# Revit family: ПЛ-10_Eng
name_source: partatom
category: Duct Accessories
units: mm (PartAtom-declared; Revit-internal decimal feet)

## family parameters
Always vertical = Yes
Cut with Voids When Loaded = No
Part Type = Attaches To
Round Connector Dimension = Use Diameter
Shared = No
Work Plane-Based = No

## types (22) — shared parameters
00_20_Manufacturer = Vents
00_20_Name = Fire-resisting damper
Apparent Load = 7 VA
Casing Material = Steel, galvanized
Frequency = 50 Hz
Load Classification = HVAC
Maintenance zone material = <By Category>
Manufacturer = Vents
Number of Fase = 1
URL = https://ventilation-system.com
Voltage = 230 V
zero-valued in all types: Default Elevation

## per-type parameters (varying)
| type | B | D | D1 | D2 | Diameter | Height | L | Length | Maximum Air Flow | R | Weight | Width |
| PL-10-PVP230T-DN100/EI60 | 195 mm  [stored 0.639764 ft] | 99 mm  [stored 0.324803 ft] | 100 mm  [stored 0.328084 ft] | 95 mm | 99 mm  [stored 0.324803 ft] | 99 mm  [stored 0.324803 ft] | 300 mm | 300 mm | 32400.0 m³/h | 50 mm  [stored 0.164042 ft] | 2.90 kg | 195 mm  [stored 0.639764 ft] |
| PL-10-PVP230T-DN400/EI60 | 505 mm | 399 mm | 400 mm | 395 mm | 399 mm | 399 mm | 310 mm  [stored 1.01706 ft] | 310 mm  [stored 1.01706 ft] | 0.0 m³/h | 200 mm  [stored 0.656168 ft] | 9.90 kg | 505 mm |
| PL-10-PVP230T-DN100/EI120 | 195 mm  [stored 0.639764 ft] | 99 mm  [stored 0.324803 ft] | 100 mm  [stored 0.328084 ft] | 95 mm | 99 mm  [stored 0.324803 ft] | 99 mm  [stored 0.324803 ft] | 300 mm | 300 mm | 0.0 m³/h | 50 mm  [stored 0.164042 ft] | 2.90 kg | 195 mm  [stored 0.639764 ft] |
| PL-10-PVP230T-DN400/EI120 | 505 mm | 399 mm | 400 mm | 395 mm | 399 mm | 399 mm | 310 mm  [stored 1.01706 ft] | 310 mm  [stored 1.01706 ft] | 0.0 m³/h | 200 mm  [stored 0.656168 ft] | 9.90 kg | 505 mm |
| PL-10-PVP230T-DN125/EI60 | 215 mm | 124 mm  [stored 0.406824 ft] | 125 mm  [stored 0.410105 ft] | 120 mm  [stored 0.393701 ft] | 124 mm  [stored 0.406824 ft] | 124 mm  [stored 0.406824 ft] | 300 mm | 300 mm | 0.0 m³/h | 62 mm  [stored 0.203412 ft] | 3.10 kg | 215 mm |
| PL-10-PVP230T-DN125/EI120 | 215 mm | 124 mm  [stored 0.406824 ft] | 125 mm  [stored 0.410105 ft] | 120 mm  [stored 0.393701 ft] | 124 mm  [stored 0.406824 ft] | 124 mm  [stored 0.406824 ft] | 300 mm | 300 mm | 0.0 m³/h | 62 mm  [stored 0.203412 ft] | 3.10 kg | 215 mm |
| PL-10-PVP230T-DN150/EI60 | 245 mm  [stored 0.803806 ft] | 149 mm  [stored 0.488845 ft] | 150 mm | 145 mm  [stored 0.475722 ft] | 149 mm  [stored 0.488845 ft] | 149 mm  [stored 0.488845 ft] | 300 mm | 300 mm | 0.0 m³/h | 75 mm | 3.40 kg | 245 mm  [stored 0.803806 ft] |
| PL-10-PVP230T-DN150/EI120 | 245 mm  [stored 0.803806 ft] | 149 mm  [stored 0.488845 ft] | 150 mm | 145 mm  [stored 0.475722 ft] | 149 mm  [stored 0.488845 ft] | 149 mm  [stored 0.488845 ft] | 300 mm | 300 mm | 0.0 m³/h | 75 mm | 3.40 kg | 245 mm  [stored 0.803806 ft] |
| PL-10-PVP230T-DN160/EI120 | 255 mm  [stored 0.836614 ft] | 159 mm  [stored 0.521654 ft] | 160 mm  [stored 0.524934 ft] | 155 mm  [stored 0.50853 ft] | 159 mm  [stored 0.521654 ft] | 159 mm  [stored 0.521654 ft] | 300 mm | 300 mm | 0.0 m³/h | 80 mm | 3.50 kg | 255 mm  [stored 0.836614 ft] |
| PL-10-PVP230T-DN180/EI120 | 275 mm | 179 mm  [stored 0.58727 ft] | 180 mm  [stored 0.590551 ft] | 175 mm  [stored 0.574147 ft] | 179 mm  [stored 0.58727 ft] | 179 mm  [stored 0.58727 ft] | 300 mm | 300 mm | 0.0 m³/h | 90 mm | 3.80 kg | 275 mm |
| PL-10-PVP230T-DN160/EI60 | 255 mm  [stored 0.836614 ft] | 159 mm  [stored 0.521654 ft] | 160 mm  [stored 0.524934 ft] | 155 mm  [stored 0.50853 ft] | 159 mm  [stored 0.521654 ft] | 159 mm  [stored 0.521654 ft] | 300 mm | 300 mm | 0.0 m³/h | 80 mm | 3.50 kg | 255 mm  [stored 0.836614 ft] |
| PL-10-PVP230T-DN180/EI60 | 275 mm | 179 mm  [stored 0.58727 ft] | 180 mm  [stored 0.590551 ft] | 175 mm  [stored 0.574147 ft] | 179 mm  [stored 0.58727 ft] | 179 mm  [stored 0.58727 ft] | 300 mm | 300 mm | 0.0 m³/h | 90 mm | 3.80 kg | 275 mm |
| PL-10-PVP230T-DN200/EI120 | 295 mm  [stored 0.967848 ft] | 199 mm  [stored 0.652887 ft] | 200 mm  [stored 0.656168 ft] | 195 mm  [stored 0.639764 ft] | 199 mm  [stored 0.652887 ft] | 199 mm  [stored 0.652887 ft] | 300 mm | 300 mm | 0.0 m³/h | 100 mm  [stored 0.328084 ft] | 4.00 kg | 295 mm  [stored 0.967848 ft] |
| PL-10-PVP230T-DN200/EI60 | 295 mm  [stored 0.967848 ft] | 199 mm  [stored 0.652887 ft] | 200 mm  [stored 0.656168 ft] | 195 mm  [stored 0.639764 ft] | 199 mm  [stored 0.652887 ft] | 199 mm  [stored 0.652887 ft] | 300 mm | 300 mm | 0.0 m³/h | 100 mm  [stored 0.328084 ft] | 4.00 kg | 295 mm  [stored 0.967848 ft] |
| PL-10-PVP230T-DN225/EI120 | 325 mm | 224 mm  [stored 0.734908 ft] | 225 mm  [stored 0.738189 ft] | 220 mm  [stored 0.721785 ft] | 224 mm  [stored 0.734908 ft] | 224 mm  [stored 0.734908 ft] | 300 mm | 300 mm | 0.0 m³/h | 112 mm  [stored 0.367454 ft] | 4.40 kg | 325 mm |
| PL-10-PVP230T-DN225/EI60 | 325 mm | 224 mm  [stored 0.734908 ft] | 225 mm  [stored 0.738189 ft] | 220 mm  [stored 0.721785 ft] | 224 mm  [stored 0.734908 ft] | 224 mm  [stored 0.734908 ft] | 300 mm | 300 mm | 0.0 m³/h | 112 mm  [stored 0.367454 ft] | 4.40 kg | 325 mm |
| PL-10-PVP230T-DN250/EI120 | 345 mm | 249 mm  [stored 0.816929 ft] | 250 mm  [stored 0.82021 ft] | 245 mm  [stored 0.803806 ft] | 249 mm  [stored 0.816929 ft] | 249 mm  [stored 0.816929 ft] | 310 mm  [stored 1.01706 ft] | 310 mm  [stored 1.01706 ft] | 0.0 m³/h | 125 mm  [stored 0.410105 ft] | 4.70 kg | 345 mm |
| PL-10-PVP230T-DN250/EI60 | 345 mm | 249 mm  [stored 0.816929 ft] | 250 mm  [stored 0.82021 ft] | 245 mm  [stored 0.803806 ft] | 249 mm  [stored 0.816929 ft] | 249 mm  [stored 0.816929 ft] | 310 mm  [stored 1.01706 ft] | 310 mm  [stored 1.01706 ft] | 0.0 m³/h | 125 mm  [stored 0.410105 ft] | 4.70 kg | 345 mm |
| PL-10-PVP230T-DN315/EI120 | 415 mm | 314 mm  [stored 1.03018 ft] | 315 mm | 310 mm  [stored 1.01706 ft] | 314 mm  [stored 1.03018 ft] | 314 mm  [stored 1.03018 ft] | 310 mm  [stored 1.01706 ft] | 310 mm  [stored 1.01706 ft] | 0.0 m³/h | 157 mm  [stored 0.515092 ft] | 6.50 kg | 415 mm |
| PL-10-PVP230T-DN315/EI60 | 415 mm | 314 mm  [stored 1.03018 ft] | 315 mm | 310 mm  [stored 1.01706 ft] | 314 mm  [stored 1.03018 ft] | 314 mm  [stored 1.03018 ft] | 310 mm  [stored 1.01706 ft] | 310 mm  [stored 1.01706 ft] | 0.0 m³/h | 157 mm  [stored 0.515092 ft] | 6.50 kg | 415 mm |
| PL-10-PVP230T-DN355/EI120 | 455 mm | 354 mm | 355 mm | 350 mm | 354 mm | 354 mm | 310 mm  [stored 1.01706 ft] | 310 mm  [stored 1.01706 ft] | 0.0 m³/h | 177 mm  [stored 0.580709 ft] | 8.30 kg | 455 mm |
| PL-10-PVP230T-DN355/EI60 | 455 mm | 354 mm | 355 mm | 350 mm | 354 mm | 354 mm | 310 mm  [stored 1.01706 ft] | 310 mm  [stored 1.01706 ft] | 0.0 m³/h | 177 mm  [stored 0.580709 ft] | 8.30 kg | 455 mm |

note: column(s) folded — value = type name in every type: 00_20_Type

note: [stored X ft] marks values corroborated as IEEE doubles in the binary element streams (Revit-internal decimal feet)
